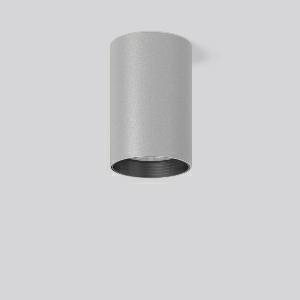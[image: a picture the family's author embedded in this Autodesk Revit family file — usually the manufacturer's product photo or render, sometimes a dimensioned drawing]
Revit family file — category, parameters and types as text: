
# Revit family: heledon_maxi_a_931228_004_3_4e05
name_source: partatom
category: Lighting Fixtures
units: mm (PartAtom-declared; Revit-internal decimal feet)

## family parameters
Cut with Voids When Loaded = No
Host = Face
Light Source = No
Part Type = Normal
Room Calculation Point = No
Round Connector Dimension = Use Diameter
Shared = No

## types (1)
- HELEDON maxi A (1 x LED Modul 935, 3600 lm, 3500)
    Apparent Load = 35 VA
    Approval mark = CE
    CIE Flux Codes = 96 100 100 100 100
    Color Rendering = 92
    Color Temperature = 3500
    Default Elevation = 1800 mm
    Description = Series: HELEDON maxi
Cylindrical surface-mounted downlight. Housing: die-cast aluminium, powder-coated. Internal ceiling frame polycarbonate with bayonet mounting. Black plastic ring and recessed LED to prevent glare from the side. Optical assembly with lens made of plastic (polycarbonate) for the best homogeneous light distribution - can be changed without tools. Best colour rendering index Ra>90. Suitable for Ceiling mounting. Easy installation with a separate ceiling frame with bayonet mounting and plug connection. Driver integrated. Connected via plug-in connector. High quality converter without flickering and stroboscopic effect. The following accessories can be mounted without use of tools: interchangeable lenses, decorative glasses, honeycomb louvre, clear and frosted diffusers, white interchangeable plastic ring. 
Colour: silver
Diameter: 123 mm
Height: 183 mm
Lamp: LED
Socket: without socket
Colour temperature: 3500K
Colour rendering index (CRI): 92
System power: 35 W
Rated luminous flux: 3600 lm
Luminous efficiency: 103 lm/W
Control gear: Regulated power supply
Protection class: I
Type of protection: IP 20
    Height = 183 mm
    Lamp = 1 x LED Modul 935
    Lamp Light Flux = 3600 lm
    Lamp count = 1
    Length = 123 mm
    Lifetime = 50000 h
    Luminous efficacy = 103 lm/W
    Manufacturer = RZB
    ModVariant = No
    Model = 931228.004.3
    Mounting Place = Ceiling
    Mounting Type = Surface mounted
    Number of Poles = 1
    OnlyDefault = Yes
    Power Factor = 1
    Product Name = HELEDON maxi A
    Product group = Surface mounted downlights
    ProductGroupID = 302
    Protection Class = Protection class I
    Protection Degree = IP 20
    RLX_Detail_Level = 1
    RLX_Emergency_Light_Flux = 0 lm
    RLX_Emergency_Type = 0
    RLX_Emergency_Type_DB = No
    RlxData = <blob elided: 98989 chars, md5=32ca2870>
    Socket = socket
    Standby Power = 0 W
    System Light Flux = 3600 lm
    System Power = 35 W
    Type Comments = Product without accessories
    Type Image = 931193.004.jpg
    URL = http://relux.com
    VarID = ---
    Voltage = 230 V
    Voltage Range = 220-240 V
    Weight = 0.00 kg
    Width = 0 mm  [stored 0 ft]

note: [stored X ft] marks values corroborated as IEEE doubles in the binary element streams (Revit-internal decimal feet)

## geometry (parser evidence)
native form markers: Blend x4, Sweep x10
no freeform markers — native parametric forms only
